# Revit family: 62025-62025450-400
name_source: partatom
category: Plumbing Fixtures
units: mm (PartAtom-declared; Revit-internal decimal feet)

## family parameters
Always vertical = Yes
Cut with Voids When Loaded = No
OmniClass Number = 23.45.00.00
OmniClass Title = Sanitary, Laundry, and Cleaning Equipment
Part Type = Valve - Breaks Into
Room Calculation Point = No
Round Connector Dimension = Use Diameter
Shared = Yes
Work Plane-Based = No

## types (1)
- toilet combinations-hansgrohe-62025XXX-EluPura S Wall hung WC Set 540 rimless AquaHelix Flush with WC seat and cover wit
    ARTNR = 62025450
    BASENUMBER = 62025
    BIMOBJECT = Sanitary: Toilets
    CATALOG = Hansgrohe
    COLLECTION = toilet combinations
    COLLECTIONSET = EluPura S
    DEPTH = 540
    DESIGN = Germany
    GTINCODE = 4059625420942
    HEIGHT = 445
    IDNR = 1
    IFC = Furnishing element
    LINA = toilet combinations-hansgrohe-62025XXX-EluPura S Wall hung WC Set 540 rimless AquaHelix Flush with WC seat and cover with SoftClose and QuickRelease, Slim, HygieneEffect
    LODLEVEL = 400
    Manufacturer = Hansgrohe
    Model = toilet combinations-hansgrohe-62025XXX-EluPura S Wall hung WC Set 540 rimless AquaHelix Flush with WC seat and cover with SoftClose and QuickRelease, Slim, HygieneEffect
    NAME = EluPura S Wall hung WC Set 540 rimless AquaHelix Flush with WC seat and cover with SoftClose and QuickRelease, Slim, HygieneEffect
    NB = 62025-62025450-400
    NBSYN = $BASENUMBER.-$ARTNR.-$LODLEVEL.
    NN = EluPura S Wall hung WC Set 540 rimless AquaHelix Flush with WC seat and cover with SoftClose and QuickRelease, Slim, HygieneEffect
    OBJECTTYPE = Object (single object)
    OMNICLASS = 23-31 19 00 | Toilets
    PERMALINK = 62025XXX
    PRODUCTURL = https://pro.hansgrohe.com
    REGIONSET = Worldwide
    SPECIFICATION = Surfaces:  - 62025450 White   Specification:  • consists of: WC, WC seat and cover, WC cover  • material: ceramic  • Made to fit NoiseReduction: customized soundproofing mat included • degree of gloss: glossy  • type: Wall hung WC Set  • with concealed siphon • rimless • HygieneEffect - reduces the spread of coliform bacteria and salmonella (Escherichia coli ATCC8739/Salmonella enterica ATCC 13076. Test: ISO 22196: 2011-08) • easy handling via push button • AquaHelix Flush: water vortex technology for optimal flushing • flushing type: wash-down  • installation type: wall-mounted  • concealed fastening for the WC • water connection: rear  • with soft-close mechanism • QuickRelease: quick removable toilet seat and cover
    SURFACE = white
    UNICLASS2015 = Pr_40_20_93_94 | WC pans
    UNICLASS_2015_CODE = 40_20_93_94
    WEIGHT = 22
    WIDTH = 366

## geometry (parser evidence)
native form markers: Sweep x16
no freeform markers — native parametric forms only
